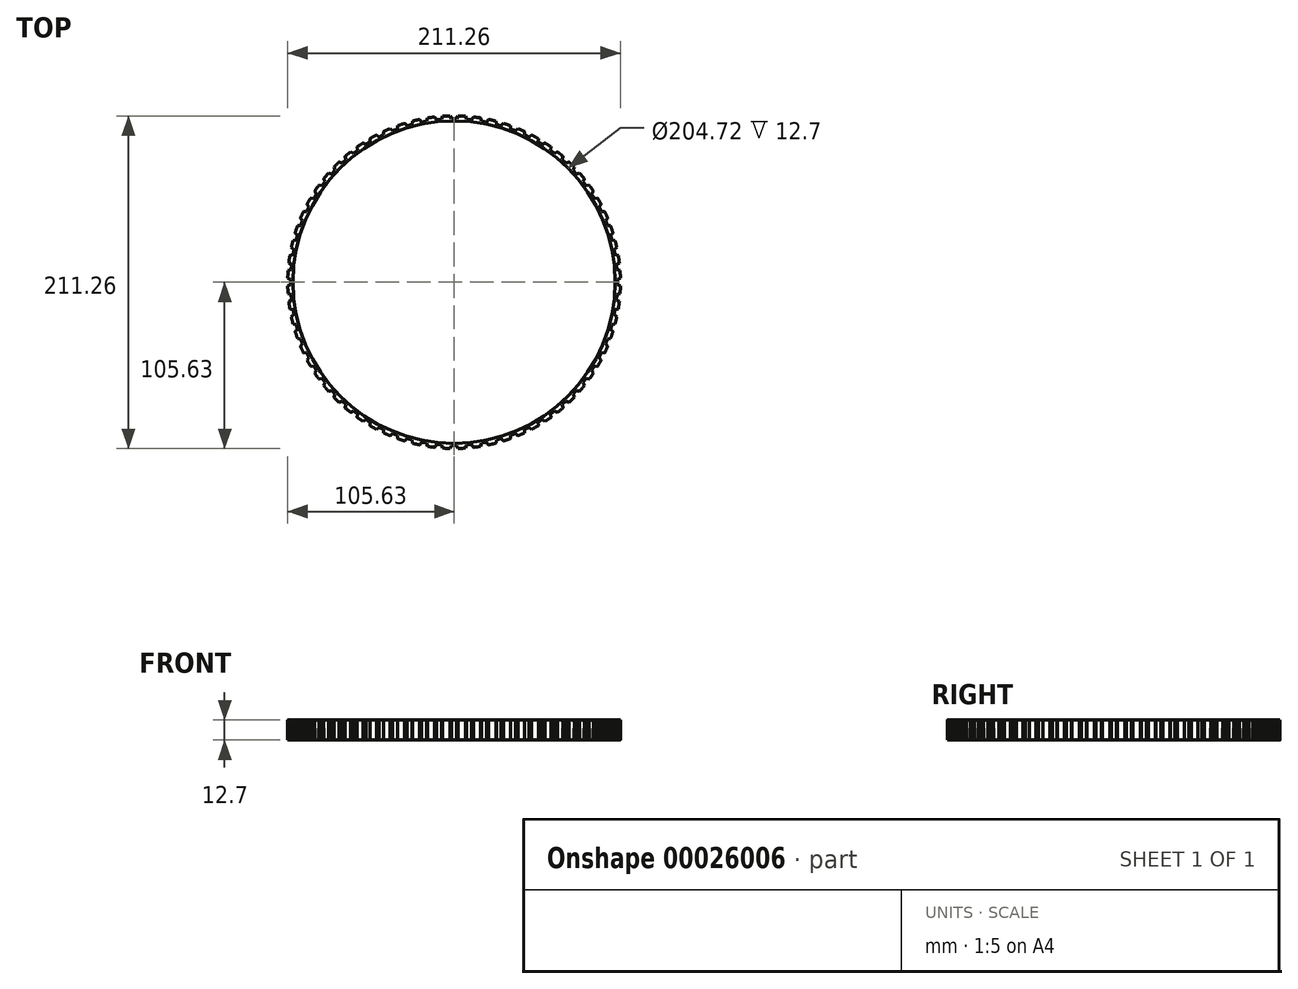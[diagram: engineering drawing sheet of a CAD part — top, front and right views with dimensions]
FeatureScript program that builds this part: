
annotation { "Feature Type Name" : "Feature", "Feature Type Description" : "" }
export const myFeature = defineFeature(function(context is Context, id is Id, definition is map)
    precondition{}
    {
        {
            var Q0;
            Q0=qCreatedBy(makeId("Top.planeOp"),FACE);
            var sketch = newSketch(context, id + "F0", { "sketchPlane" : qUnion([Q0])});
            skCircle(sketch, "E0", {"center": v(0, 0) * mm, "radius": 103.76 * mm, "construction": true});
            skCircle(sketch, "E1", {"center": v(0, 0) * mm, "radius": 102.36 * mm});
            skCircle(sketch, "E2", {"center": v(0, 0) * mm, "radius": 105.66 * mm});
            skSolve(sketch);
        }
        {
            var Q0;
            Q0=qSketchRegion(id+"F0",true);
            extrude(context, id + "F1", {"entities" : qUnion([Q0]), "depth" : 12.7 * mm});
        }
        {
            var Q0;
            Q0=makeQuery(id+"F1.opExtrude","CAP_FACE",FACE,{"disambiguationData":[OSD([sQuery(id+"F0.wireOp",EDGE,"E1"),sQuery(id+"F0.wireOp",EDGE,"E2")])],"isStart":false});
            var sketch = newSketch(context, id + "F2", { "sketchPlane" : qUnion([Q0])});
            skLineSegment(sketch, "E3", {"start": v(0, 0) * mm, "end": v(0, 103.76) * mm, "construction": true});
            skLineSegment(sketch, "E4", {"start": v(-1.63, 103.76) * mm, "end": v(1.63, 103.76) * mm});
            skLineSegment(sketch, "E5", {"start": v(-1.63, 103.76) * mm, "end": v(-3.2, 107.13) * mm});
            skLineSegment(sketch, "E6", {"start": v(1.63, 103.76) * mm, "end": v(3.2, 107.13) * mm});
            skLineSegment(sketch, "E7", {"start": v(3.2, 107.13) * mm, "end": v(-3.2, 107.13) * mm});
            skLineSegment(sketch, "E8", {"start": v(0, 103.76) * mm, "end": v(0, 107.13) * mm, "construction": true});
            skLineSegment(sketch, "E9.1.2", {"start": v(-11.2, 103.17) * mm, "end": v(-13.07, 106.38) * mm});
            skLineSegment(sketch, "E9.1.3", {"start": v(-11.2, 103.17) * mm, "end": v(-7.96, 103.47) * mm});
            skLineSegment(sketch, "E9.1.7", {"start": v(-7.96, 103.47) * mm, "end": v(-6.7, 106.97) * mm});
            skLineSegment(sketch, "E9.1.8", {"start": v(-6.7, 106.97) * mm, "end": v(-13.07, 106.38) * mm});
            skLineSegment(sketch, "E9.2.2", {"start": v(-20.66, 101.7) * mm, "end": v(-22.83, 104.72) * mm});
            skLineSegment(sketch, "E9.2.3", {"start": v(-20.66, 101.7) * mm, "end": v(-17.47, 102.3) * mm});
            skLineSegment(sketch, "E9.2.7", {"start": v(-17.47, 102.3) * mm, "end": v(-16.54, 105.9) * mm});
            skLineSegment(sketch, "E9.2.8", {"start": v(-16.54, 105.9) * mm, "end": v(-22.83, 104.72) * mm});
            skLineSegment(sketch, "E9.3.2", {"start": v(-29.96, 99.35) * mm, "end": v(-32.4, 102.17) * mm});
            skLineSegment(sketch, "E9.3.3", {"start": v(-29.96, 99.35) * mm, "end": v(-26.83, 100.24) * mm});
            skLineSegment(sketch, "E9.3.7", {"start": v(-26.83, 100.24) * mm, "end": v(-26.24, 103.92) * mm});
            skLineSegment(sketch, "E9.3.8", {"start": v(-26.24, 103.92) * mm, "end": v(-32.4, 102.17) * mm});
            skLineSegment(sketch, "E9.4.2", {"start": v(-39, 96.17) * mm, "end": v(-41.68, 98.74) * mm});
            skLineSegment(sketch, "E9.4.3", {"start": v(-39, 96.17) * mm, "end": v(-35.97, 97.34) * mm});
            skLineSegment(sketch, "E9.4.7", {"start": v(-35.97, 97.34) * mm, "end": v(-35.72, 101.05) * mm});
            skLineSegment(sketch, "E9.4.8", {"start": v(-35.72, 101.05) * mm, "end": v(-41.68, 98.74) * mm});
            skLineSegment(sketch, "E9.5.2", {"start": v(-47.7, 92.16) * mm, "end": v(-50.61, 94.47) * mm});
            skLineSegment(sketch, "E9.5.3", {"start": v(-47.7, 92.16) * mm, "end": v(-44.8, 93.6) * mm});
            skLineSegment(sketch, "E9.5.7", {"start": v(-44.8, 93.6) * mm, "end": v(-44.89, 97.32) * mm});
            skLineSegment(sketch, "E9.5.8", {"start": v(-44.89, 97.32) * mm, "end": v(-50.61, 94.47) * mm});
            skLineSegment(sketch, "E9.6.2", {"start": v(-56, 87.36) * mm, "end": v(-59.12, 89.4) * mm});
            skLineSegment(sketch, "E9.6.3", {"start": v(-56, 87.36) * mm, "end": v(-53.24, 89.07) * mm});
            skLineSegment(sketch, "E9.6.7", {"start": v(-53.24, 89.07) * mm, "end": v(-53.68, 92.77) * mm});
            skLineSegment(sketch, "E9.6.8", {"start": v(-53.68, 92.77) * mm, "end": v(-59.12, 89.4) * mm});
            skLineSegment(sketch, "E9.7.2", {"start": v(-63.83, 81.82) * mm, "end": v(-67.11, 83.57) * mm});
            skLineSegment(sketch, "E9.7.3", {"start": v(-63.83, 81.82) * mm, "end": v(-61.23, 83.78) * mm});
            skLineSegment(sketch, "E9.7.7", {"start": v(-61.23, 83.78) * mm, "end": v(-62, 87.42) * mm});
            skLineSegment(sketch, "E9.7.8", {"start": v(-62, 87.42) * mm, "end": v(-67.11, 83.57) * mm});
            skLineSegment(sketch, "E9.8.2", {"start": v(-71.1, 75.58) * mm, "end": v(-74.54, 77.02) * mm});
            skLineSegment(sketch, "E9.8.3", {"start": v(-71.1, 75.58) * mm, "end": v(-68.7, 77.77) * mm});
            skLineSegment(sketch, "E9.8.7", {"start": v(-68.7, 77.77) * mm, "end": v(-69.81, 81.32) * mm});
            skLineSegment(sketch, "E9.8.8", {"start": v(-69.81, 81.32) * mm, "end": v(-74.54, 77.02) * mm});
            skLineSegment(sketch, "E9.9.2", {"start": v(-77.77, 68.7) * mm, "end": v(-81.32, 69.81) * mm});
            skLineSegment(sketch, "E9.9.3", {"start": v(-77.77, 68.7) * mm, "end": v(-75.58, 71.1) * mm});
            skLineSegment(sketch, "E9.9.7", {"start": v(-75.58, 71.1) * mm, "end": v(-77.02, 74.54) * mm});
            skLineSegment(sketch, "E9.9.8", {"start": v(-77.02, 74.54) * mm, "end": v(-81.32, 69.81) * mm});
            skLineSegment(sketch, "E9.10.2", {"start": v(-83.78, 61.23) * mm, "end": v(-87.42, 62) * mm});
            skLineSegment(sketch, "E9.10.3", {"start": v(-83.78, 61.23) * mm, "end": v(-81.82, 63.83) * mm});
            skLineSegment(sketch, "E9.10.7", {"start": v(-81.82, 63.83) * mm, "end": v(-83.57, 67.11) * mm});
            skLineSegment(sketch, "E9.10.8", {"start": v(-83.57, 67.11) * mm, "end": v(-87.42, 62) * mm});
            skLineSegment(sketch, "E9.11.2", {"start": v(-89.07, 53.24) * mm, "end": v(-92.77, 53.68) * mm});
            skLineSegment(sketch, "E9.11.3", {"start": v(-89.07, 53.24) * mm, "end": v(-87.36, 56) * mm});
            skLineSegment(sketch, "E9.11.7", {"start": v(-87.36, 56) * mm, "end": v(-89.4, 59.12) * mm});
            skLineSegment(sketch, "E9.11.8", {"start": v(-89.4, 59.12) * mm, "end": v(-92.77, 53.68) * mm});
            skLineSegment(sketch, "E9.12.2", {"start": v(-93.6, 44.8) * mm, "end": v(-97.32, 44.89) * mm});
            skLineSegment(sketch, "E9.12.3", {"start": v(-93.6, 44.8) * mm, "end": v(-92.16, 47.7) * mm});
            skLineSegment(sketch, "E9.12.7", {"start": v(-92.16, 47.7) * mm, "end": v(-94.47, 50.61) * mm});
            skLineSegment(sketch, "E9.12.8", {"start": v(-94.47, 50.61) * mm, "end": v(-97.32, 44.89) * mm});
            skLineSegment(sketch, "E9.13.2", {"start": v(-97.34, 35.97) * mm, "end": v(-101.05, 35.72) * mm});
            skLineSegment(sketch, "E9.13.3", {"start": v(-97.34, 35.97) * mm, "end": v(-96.17, 39) * mm});
            skLineSegment(sketch, "E9.13.7", {"start": v(-96.17, 39) * mm, "end": v(-98.74, 41.68) * mm});
            skLineSegment(sketch, "E9.13.8", {"start": v(-98.74, 41.68) * mm, "end": v(-101.05, 35.72) * mm});
            skLineSegment(sketch, "E9.14.2", {"start": v(-100.24, 26.83) * mm, "end": v(-103.92, 26.24) * mm});
            skLineSegment(sketch, "E9.14.3", {"start": v(-100.24, 26.83) * mm, "end": v(-99.35, 29.96) * mm});
            skLineSegment(sketch, "E9.14.7", {"start": v(-99.35, 29.96) * mm, "end": v(-102.17, 32.4) * mm});
            skLineSegment(sketch, "E9.14.8", {"start": v(-102.17, 32.4) * mm, "end": v(-103.92, 26.24) * mm});
            skLineSegment(sketch, "E9.15.2", {"start": v(-102.3, 17.47) * mm, "end": v(-105.9, 16.54) * mm});
            skLineSegment(sketch, "E9.15.3", {"start": v(-102.3, 17.47) * mm, "end": v(-101.7, 20.66) * mm});
            skLineSegment(sketch, "E9.15.7", {"start": v(-101.7, 20.66) * mm, "end": v(-104.72, 22.83) * mm});
            skLineSegment(sketch, "E9.15.8", {"start": v(-104.72, 22.83) * mm, "end": v(-105.9, 16.54) * mm});
            skLineSegment(sketch, "E9.16.2", {"start": v(-103.47, 7.96) * mm, "end": v(-106.97, 6.7) * mm});
            skLineSegment(sketch, "E9.16.3", {"start": v(-103.47, 7.96) * mm, "end": v(-103.17, 11.2) * mm});
            skLineSegment(sketch, "E9.16.7", {"start": v(-103.17, 11.2) * mm, "end": v(-106.38, 13.07) * mm});
            skLineSegment(sketch, "E9.16.8", {"start": v(-106.38, 13.07) * mm, "end": v(-106.97, 6.7) * mm});
            skLineSegment(sketch, "E9.17.2", {"start": v(-103.76, -1.63) * mm, "end": v(-107.13, -3.2) * mm});
            skLineSegment(sketch, "E9.17.3", {"start": v(-103.76, -1.63) * mm, "end": v(-103.76, 1.63) * mm});
            skLineSegment(sketch, "E9.17.7", {"start": v(-103.76, 1.63) * mm, "end": v(-107.13, 3.2) * mm});
            skLineSegment(sketch, "E9.17.8", {"start": v(-107.13, 3.2) * mm, "end": v(-107.13, -3.2) * mm});
            skLineSegment(sketch, "E9.18.2", {"start": v(-103.17, -11.2) * mm, "end": v(-106.38, -13.07) * mm});
            skLineSegment(sketch, "E9.18.3", {"start": v(-103.17, -11.2) * mm, "end": v(-103.47, -7.96) * mm});
            skLineSegment(sketch, "E9.18.7", {"start": v(-103.47, -7.96) * mm, "end": v(-106.97, -6.7) * mm});
            skLineSegment(sketch, "E9.18.8", {"start": v(-106.97, -6.7) * mm, "end": v(-106.38, -13.07) * mm});
            skLineSegment(sketch, "E9.19.2", {"start": v(-101.7, -20.66) * mm, "end": v(-104.72, -22.83) * mm});
            skLineSegment(sketch, "E9.19.3", {"start": v(-101.7, -20.66) * mm, "end": v(-102.3, -17.47) * mm});
            skLineSegment(sketch, "E9.19.7", {"start": v(-102.3, -17.47) * mm, "end": v(-105.9, -16.54) * mm});
            skLineSegment(sketch, "E9.19.8", {"start": v(-105.9, -16.54) * mm, "end": v(-104.72, -22.83) * mm});
            skLineSegment(sketch, "E9.20.2", {"start": v(-99.35, -29.96) * mm, "end": v(-102.17, -32.4) * mm});
            skLineSegment(sketch, "E9.20.3", {"start": v(-99.35, -29.96) * mm, "end": v(-100.24, -26.83) * mm});
            skLineSegment(sketch, "E9.20.7", {"start": v(-100.24, -26.83) * mm, "end": v(-103.92, -26.24) * mm});
            skLineSegment(sketch, "E9.20.8", {"start": v(-103.92, -26.24) * mm, "end": v(-102.17, -32.4) * mm});
            skLineSegment(sketch, "E9.21.2", {"start": v(-96.17, -39) * mm, "end": v(-98.74, -41.68) * mm});
            skLineSegment(sketch, "E9.21.3", {"start": v(-96.17, -39) * mm, "end": v(-97.34, -35.97) * mm});
            skLineSegment(sketch, "E9.21.7", {"start": v(-97.34, -35.97) * mm, "end": v(-101.05, -35.72) * mm});
            skLineSegment(sketch, "E9.21.8", {"start": v(-101.05, -35.72) * mm, "end": v(-98.74, -41.68) * mm});
            skLineSegment(sketch, "E9.22.2", {"start": v(-92.16, -47.7) * mm, "end": v(-94.47, -50.61) * mm});
            skLineSegment(sketch, "E9.22.3", {"start": v(-92.16, -47.7) * mm, "end": v(-93.6, -44.8) * mm});
            skLineSegment(sketch, "E9.22.7", {"start": v(-93.6, -44.8) * mm, "end": v(-97.32, -44.89) * mm});
            skLineSegment(sketch, "E9.22.8", {"start": v(-97.32, -44.89) * mm, "end": v(-94.47, -50.61) * mm});
            skLineSegment(sketch, "E9.23.2", {"start": v(-87.36, -56) * mm, "end": v(-89.4, -59.12) * mm});
            skLineSegment(sketch, "E9.23.3", {"start": v(-87.36, -56) * mm, "end": v(-89.07, -53.24) * mm});
            skLineSegment(sketch, "E9.23.7", {"start": v(-89.07, -53.24) * mm, "end": v(-92.77, -53.68) * mm});
            skLineSegment(sketch, "E9.23.8", {"start": v(-92.77, -53.68) * mm, "end": v(-89.4, -59.12) * mm});
            skLineSegment(sketch, "E9.24.2", {"start": v(-81.82, -63.83) * mm, "end": v(-83.57, -67.11) * mm});
            skLineSegment(sketch, "E9.24.3", {"start": v(-81.82, -63.83) * mm, "end": v(-83.78, -61.23) * mm});
            skLineSegment(sketch, "E9.24.7", {"start": v(-83.78, -61.23) * mm, "end": v(-87.42, -62) * mm});
            skLineSegment(sketch, "E9.24.8", {"start": v(-87.42, -62) * mm, "end": v(-83.57, -67.11) * mm});
            skLineSegment(sketch, "E9.25.2", {"start": v(-75.58, -71.1) * mm, "end": v(-77.02, -74.54) * mm});
            skLineSegment(sketch, "E9.25.3", {"start": v(-75.58, -71.1) * mm, "end": v(-77.77, -68.7) * mm});
            skLineSegment(sketch, "E9.25.7", {"start": v(-77.77, -68.7) * mm, "end": v(-81.32, -69.81) * mm});
            skLineSegment(sketch, "E9.25.8", {"start": v(-81.32, -69.81) * mm, "end": v(-77.02, -74.54) * mm});
            skLineSegment(sketch, "E9.26.2", {"start": v(-68.7, -77.77) * mm, "end": v(-69.81, -81.32) * mm});
            skLineSegment(sketch, "E9.26.3", {"start": v(-68.7, -77.77) * mm, "end": v(-71.1, -75.58) * mm});
            skLineSegment(sketch, "E9.26.7", {"start": v(-71.1, -75.58) * mm, "end": v(-74.54, -77.02) * mm});
            skLineSegment(sketch, "E9.26.8", {"start": v(-74.54, -77.02) * mm, "end": v(-69.81, -81.32) * mm});
            skLineSegment(sketch, "E9.27.2", {"start": v(-61.23, -83.78) * mm, "end": v(-62, -87.42) * mm});
            skLineSegment(sketch, "E9.27.3", {"start": v(-61.23, -83.78) * mm, "end": v(-63.83, -81.82) * mm});
            skLineSegment(sketch, "E9.27.7", {"start": v(-63.83, -81.82) * mm, "end": v(-67.11, -83.57) * mm});
            skLineSegment(sketch, "E9.27.8", {"start": v(-67.11, -83.57) * mm, "end": v(-62, -87.42) * mm});
            skLineSegment(sketch, "E9.28.2", {"start": v(-53.24, -89.07) * mm, "end": v(-53.68, -92.77) * mm});
            skLineSegment(sketch, "E9.28.3", {"start": v(-53.24, -89.07) * mm, "end": v(-56, -87.36) * mm});
            skLineSegment(sketch, "E9.28.7", {"start": v(-56, -87.36) * mm, "end": v(-59.12, -89.4) * mm});
            skLineSegment(sketch, "E9.28.8", {"start": v(-59.12, -89.4) * mm, "end": v(-53.68, -92.77) * mm});
            skLineSegment(sketch, "E9.29.2", {"start": v(-44.8, -93.6) * mm, "end": v(-44.89, -97.32) * mm});
            skLineSegment(sketch, "E9.29.3", {"start": v(-44.8, -93.6) * mm, "end": v(-47.7, -92.16) * mm});
            skLineSegment(sketch, "E9.29.7", {"start": v(-47.7, -92.16) * mm, "end": v(-50.61, -94.47) * mm});
            skLineSegment(sketch, "E9.29.8", {"start": v(-50.61, -94.47) * mm, "end": v(-44.89, -97.32) * mm});
            skLineSegment(sketch, "E9.30.2", {"start": v(-35.97, -97.34) * mm, "end": v(-35.72, -101.05) * mm});
            skLineSegment(sketch, "E9.30.3", {"start": v(-35.97, -97.34) * mm, "end": v(-39, -96.17) * mm});
            skLineSegment(sketch, "E9.30.7", {"start": v(-39, -96.17) * mm, "end": v(-41.68, -98.74) * mm});
            skLineSegment(sketch, "E9.30.8", {"start": v(-41.68, -98.74) * mm, "end": v(-35.72, -101.05) * mm});
            skLineSegment(sketch, "E9.31.2", {"start": v(-26.83, -100.24) * mm, "end": v(-26.24, -103.92) * mm});
            skLineSegment(sketch, "E9.31.3", {"start": v(-26.83, -100.24) * mm, "end": v(-29.96, -99.35) * mm});
            skLineSegment(sketch, "E9.31.7", {"start": v(-29.96, -99.35) * mm, "end": v(-32.4, -102.17) * mm});
            skLineSegment(sketch, "E9.31.8", {"start": v(-32.4, -102.17) * mm, "end": v(-26.24, -103.92) * mm});
            skLineSegment(sketch, "E9.32.2", {"start": v(-17.47, -102.3) * mm, "end": v(-16.54, -105.9) * mm});
            skLineSegment(sketch, "E9.32.3", {"start": v(-17.47, -102.3) * mm, "end": v(-20.66, -101.7) * mm});
            skLineSegment(sketch, "E9.32.7", {"start": v(-20.66, -101.7) * mm, "end": v(-22.83, -104.72) * mm});
            skLineSegment(sketch, "E9.32.8", {"start": v(-22.83, -104.72) * mm, "end": v(-16.54, -105.9) * mm});
            skLineSegment(sketch, "E9.33.2", {"start": v(-7.96, -103.47) * mm, "end": v(-6.7, -106.97) * mm});
            skLineSegment(sketch, "E9.33.3", {"start": v(-7.96, -103.47) * mm, "end": v(-11.2, -103.17) * mm});
            skLineSegment(sketch, "E9.33.7", {"start": v(-11.2, -103.17) * mm, "end": v(-13.07, -106.38) * mm});
            skLineSegment(sketch, "E9.33.8", {"start": v(-13.07, -106.38) * mm, "end": v(-6.7, -106.97) * mm});
            skLineSegment(sketch, "E9.34.2", {"start": v(1.63, -103.76) * mm, "end": v(3.2, -107.13) * mm});
            skLineSegment(sketch, "E9.34.3", {"start": v(1.63, -103.76) * mm, "end": v(-1.63, -103.76) * mm});
            skLineSegment(sketch, "E9.34.7", {"start": v(-1.63, -103.76) * mm, "end": v(-3.2, -107.13) * mm});
            skLineSegment(sketch, "E9.34.8", {"start": v(-3.2, -107.13) * mm, "end": v(3.2, -107.13) * mm});
            skLineSegment(sketch, "E9.35.2", {"start": v(11.2, -103.17) * mm, "end": v(13.07, -106.38) * mm});
            skLineSegment(sketch, "E9.35.3", {"start": v(11.2, -103.17) * mm, "end": v(7.96, -103.47) * mm});
            skLineSegment(sketch, "E9.35.7", {"start": v(7.96, -103.47) * mm, "end": v(6.7, -106.97) * mm});
            skLineSegment(sketch, "E9.35.8", {"start": v(6.7, -106.97) * mm, "end": v(13.07, -106.38) * mm});
            skLineSegment(sketch, "E9.36.2", {"start": v(20.66, -101.7) * mm, "end": v(22.83, -104.72) * mm});
            skLineSegment(sketch, "E9.36.3", {"start": v(20.66, -101.7) * mm, "end": v(17.47, -102.3) * mm});
            skLineSegment(sketch, "E9.36.7", {"start": v(17.47, -102.3) * mm, "end": v(16.54, -105.9) * mm});
            skLineSegment(sketch, "E9.36.8", {"start": v(16.54, -105.9) * mm, "end": v(22.83, -104.72) * mm});
            skLineSegment(sketch, "E9.37.2", {"start": v(29.96, -99.35) * mm, "end": v(32.4, -102.17) * mm});
            skLineSegment(sketch, "E9.37.3", {"start": v(29.96, -99.35) * mm, "end": v(26.83, -100.24) * mm});
            skLineSegment(sketch, "E9.37.7", {"start": v(26.83, -100.24) * mm, "end": v(26.24, -103.92) * mm});
            skLineSegment(sketch, "E9.37.8", {"start": v(26.24, -103.92) * mm, "end": v(32.4, -102.17) * mm});
            skLineSegment(sketch, "E9.38.2", {"start": v(39, -96.17) * mm, "end": v(41.68, -98.74) * mm});
            skLineSegment(sketch, "E9.38.3", {"start": v(39, -96.17) * mm, "end": v(35.97, -97.34) * mm});
            skLineSegment(sketch, "E9.38.7", {"start": v(35.97, -97.34) * mm, "end": v(35.72, -101.05) * mm});
            skLineSegment(sketch, "E9.38.8", {"start": v(35.72, -101.05) * mm, "end": v(41.68, -98.74) * mm});
            skLineSegment(sketch, "E9.39.2", {"start": v(47.7, -92.16) * mm, "end": v(50.61, -94.47) * mm});
            skLineSegment(sketch, "E9.39.3", {"start": v(47.7, -92.16) * mm, "end": v(44.8, -93.6) * mm});
            skLineSegment(sketch, "E9.39.7", {"start": v(44.8, -93.6) * mm, "end": v(44.89, -97.32) * mm});
            skLineSegment(sketch, "E9.39.8", {"start": v(44.89, -97.32) * mm, "end": v(50.61, -94.47) * mm});
            skLineSegment(sketch, "E9.40.2", {"start": v(56, -87.36) * mm, "end": v(59.12, -89.4) * mm});
            skLineSegment(sketch, "E9.40.3", {"start": v(56, -87.36) * mm, "end": v(53.24, -89.07) * mm});
            skLineSegment(sketch, "E9.40.7", {"start": v(53.24, -89.07) * mm, "end": v(53.68, -92.77) * mm});
            skLineSegment(sketch, "E9.40.8", {"start": v(53.68, -92.77) * mm, "end": v(59.12, -89.4) * mm});
            skLineSegment(sketch, "E9.41.2", {"start": v(63.83, -81.82) * mm, "end": v(67.11, -83.57) * mm});
            skLineSegment(sketch, "E9.41.3", {"start": v(63.83, -81.82) * mm, "end": v(61.23, -83.78) * mm});
            skLineSegment(sketch, "E9.41.7", {"start": v(61.23, -83.78) * mm, "end": v(62, -87.42) * mm});
            skLineSegment(sketch, "E9.41.8", {"start": v(62, -87.42) * mm, "end": v(67.11, -83.57) * mm});
            skLineSegment(sketch, "E9.42.2", {"start": v(71.1, -75.58) * mm, "end": v(74.54, -77.02) * mm});
            skLineSegment(sketch, "E9.42.3", {"start": v(71.1, -75.58) * mm, "end": v(68.7, -77.77) * mm});
            skLineSegment(sketch, "E9.42.7", {"start": v(68.7, -77.77) * mm, "end": v(69.81, -81.32) * mm});
            skLineSegment(sketch, "E9.42.8", {"start": v(69.81, -81.32) * mm, "end": v(74.54, -77.02) * mm});
            skLineSegment(sketch, "E9.43.2", {"start": v(77.77, -68.7) * mm, "end": v(81.32, -69.81) * mm});
            skLineSegment(sketch, "E9.43.3", {"start": v(77.77, -68.7) * mm, "end": v(75.58, -71.1) * mm});
            skLineSegment(sketch, "E9.43.7", {"start": v(75.58, -71.1) * mm, "end": v(77.02, -74.54) * mm});
            skLineSegment(sketch, "E9.43.8", {"start": v(77.02, -74.54) * mm, "end": v(81.32, -69.81) * mm});
            skLineSegment(sketch, "E9.44.2", {"start": v(83.78, -61.23) * mm, "end": v(87.42, -62) * mm});
            skLineSegment(sketch, "E9.44.3", {"start": v(83.78, -61.23) * mm, "end": v(81.82, -63.83) * mm});
            skLineSegment(sketch, "E9.44.7", {"start": v(81.82, -63.83) * mm, "end": v(83.57, -67.11) * mm});
            skLineSegment(sketch, "E9.44.8", {"start": v(83.57, -67.11) * mm, "end": v(87.42, -62) * mm});
            skLineSegment(sketch, "E9.45.2", {"start": v(89.07, -53.24) * mm, "end": v(92.77, -53.68) * mm});
            skLineSegment(sketch, "E9.45.3", {"start": v(89.07, -53.24) * mm, "end": v(87.36, -56) * mm});
            skLineSegment(sketch, "E9.45.7", {"start": v(87.36, -56) * mm, "end": v(89.4, -59.12) * mm});
            skLineSegment(sketch, "E9.45.8", {"start": v(89.4, -59.12) * mm, "end": v(92.77, -53.68) * mm});
            skLineSegment(sketch, "E9.46.2", {"start": v(93.6, -44.8) * mm, "end": v(97.32, -44.89) * mm});
            skLineSegment(sketch, "E9.46.3", {"start": v(93.6, -44.8) * mm, "end": v(92.16, -47.7) * mm});
            skLineSegment(sketch, "E9.46.7", {"start": v(92.16, -47.7) * mm, "end": v(94.47, -50.61) * mm});
            skLineSegment(sketch, "E9.46.8", {"start": v(94.47, -50.61) * mm, "end": v(97.32, -44.89) * mm});
            skLineSegment(sketch, "E9.47.2", {"start": v(97.34, -35.97) * mm, "end": v(101.05, -35.72) * mm});
            skLineSegment(sketch, "E9.47.3", {"start": v(97.34, -35.97) * mm, "end": v(96.17, -39) * mm});
            skLineSegment(sketch, "E9.47.7", {"start": v(96.17, -39) * mm, "end": v(98.74, -41.68) * mm});
            skLineSegment(sketch, "E9.47.8", {"start": v(98.74, -41.68) * mm, "end": v(101.05, -35.72) * mm});
            skLineSegment(sketch, "E9.48.2", {"start": v(100.24, -26.83) * mm, "end": v(103.92, -26.24) * mm});
            skLineSegment(sketch, "E9.48.3", {"start": v(100.24, -26.83) * mm, "end": v(99.35, -29.96) * mm});
            skLineSegment(sketch, "E9.48.7", {"start": v(99.35, -29.96) * mm, "end": v(102.17, -32.4) * mm});
            skLineSegment(sketch, "E9.48.8", {"start": v(102.17, -32.4) * mm, "end": v(103.92, -26.24) * mm});
            skLineSegment(sketch, "E9.49.2", {"start": v(102.3, -17.47) * mm, "end": v(105.9, -16.54) * mm});
            skLineSegment(sketch, "E9.49.3", {"start": v(102.3, -17.47) * mm, "end": v(101.7, -20.66) * mm});
            skLineSegment(sketch, "E9.49.7", {"start": v(101.7, -20.66) * mm, "end": v(104.72, -22.83) * mm});
            skLineSegment(sketch, "E9.49.8", {"start": v(104.72, -22.83) * mm, "end": v(105.9, -16.54) * mm});
            skLineSegment(sketch, "E9.50.2", {"start": v(103.47, -7.96) * mm, "end": v(106.97, -6.7) * mm});
            skLineSegment(sketch, "E9.50.3", {"start": v(103.47, -7.96) * mm, "end": v(103.17, -11.2) * mm});
            skLineSegment(sketch, "E9.50.7", {"start": v(103.17, -11.2) * mm, "end": v(106.38, -13.07) * mm});
            skLineSegment(sketch, "E9.50.8", {"start": v(106.38, -13.07) * mm, "end": v(106.97, -6.7) * mm});
            skLineSegment(sketch, "E9.51.2", {"start": v(103.76, 1.63) * mm, "end": v(107.13, 3.2) * mm});
            skLineSegment(sketch, "E9.51.3", {"start": v(103.76, 1.63) * mm, "end": v(103.76, -1.63) * mm});
            skLineSegment(sketch, "E9.51.7", {"start": v(103.76, -1.63) * mm, "end": v(107.13, -3.2) * mm});
            skLineSegment(sketch, "E9.51.8", {"start": v(107.13, -3.2) * mm, "end": v(107.13, 3.2) * mm});
            skLineSegment(sketch, "E9.52.2", {"start": v(103.17, 11.2) * mm, "end": v(106.38, 13.07) * mm});
            skLineSegment(sketch, "E9.52.3", {"start": v(103.17, 11.2) * mm, "end": v(103.47, 7.96) * mm});
            skLineSegment(sketch, "E9.52.7", {"start": v(103.47, 7.96) * mm, "end": v(106.97, 6.7) * mm});
            skLineSegment(sketch, "E9.52.8", {"start": v(106.97, 6.7) * mm, "end": v(106.38, 13.07) * mm});
            skLineSegment(sketch, "E9.53.2", {"start": v(101.7, 20.66) * mm, "end": v(104.72, 22.83) * mm});
            skLineSegment(sketch, "E9.53.3", {"start": v(101.7, 20.66) * mm, "end": v(102.3, 17.47) * mm});
            skLineSegment(sketch, "E9.53.7", {"start": v(102.3, 17.47) * mm, "end": v(105.9, 16.54) * mm});
            skLineSegment(sketch, "E9.53.8", {"start": v(105.9, 16.54) * mm, "end": v(104.72, 22.83) * mm});
            skLineSegment(sketch, "E9.54.2", {"start": v(99.35, 29.96) * mm, "end": v(102.17, 32.4) * mm});
            skLineSegment(sketch, "E9.54.3", {"start": v(99.35, 29.96) * mm, "end": v(100.24, 26.83) * mm});
            skLineSegment(sketch, "E9.54.7", {"start": v(100.24, 26.83) * mm, "end": v(103.92, 26.24) * mm});
            skLineSegment(sketch, "E9.54.8", {"start": v(103.92, 26.24) * mm, "end": v(102.17, 32.4) * mm});
            skLineSegment(sketch, "E9.55.2", {"start": v(96.17, 39) * mm, "end": v(98.74, 41.68) * mm});
            skLineSegment(sketch, "E9.55.3", {"start": v(96.17, 39) * mm, "end": v(97.34, 35.97) * mm});
            skLineSegment(sketch, "E9.55.7", {"start": v(97.34, 35.97) * mm, "end": v(101.05, 35.72) * mm});
            skLineSegment(sketch, "E9.55.8", {"start": v(101.05, 35.72) * mm, "end": v(98.74, 41.68) * mm});
            skLineSegment(sketch, "E9.56.2", {"start": v(92.16, 47.7) * mm, "end": v(94.47, 50.61) * mm});
            skLineSegment(sketch, "E9.56.3", {"start": v(92.16, 47.7) * mm, "end": v(93.6, 44.8) * mm});
            skLineSegment(sketch, "E9.56.7", {"start": v(93.6, 44.8) * mm, "end": v(97.32, 44.89) * mm});
            skLineSegment(sketch, "E9.56.8", {"start": v(97.32, 44.89) * mm, "end": v(94.47, 50.61) * mm});
            skLineSegment(sketch, "E9.57.2", {"start": v(87.36, 56) * mm, "end": v(89.4, 59.12) * mm});
            skLineSegment(sketch, "E9.57.3", {"start": v(87.36, 56) * mm, "end": v(89.07, 53.24) * mm});
            skLineSegment(sketch, "E9.57.7", {"start": v(89.07, 53.24) * mm, "end": v(92.77, 53.68) * mm});
            skLineSegment(sketch, "E9.57.8", {"start": v(92.77, 53.68) * mm, "end": v(89.4, 59.12) * mm});
            skLineSegment(sketch, "E9.58.2", {"start": v(81.82, 63.83) * mm, "end": v(83.57, 67.11) * mm});
            skLineSegment(sketch, "E9.58.3", {"start": v(81.82, 63.83) * mm, "end": v(83.78, 61.23) * mm});
            skLineSegment(sketch, "E9.58.7", {"start": v(83.78, 61.23) * mm, "end": v(87.42, 62) * mm});
            skLineSegment(sketch, "E9.58.8", {"start": v(87.42, 62) * mm, "end": v(83.57, 67.11) * mm});
            skLineSegment(sketch, "E9.59.2", {"start": v(75.58, 71.1) * mm, "end": v(77.02, 74.54) * mm});
            skLineSegment(sketch, "E9.59.3", {"start": v(75.58, 71.1) * mm, "end": v(77.77, 68.7) * mm});
            skLineSegment(sketch, "E9.59.7", {"start": v(77.77, 68.7) * mm, "end": v(81.32, 69.81) * mm});
            skLineSegment(sketch, "E9.59.8", {"start": v(81.32, 69.81) * mm, "end": v(77.02, 74.54) * mm});
            skLineSegment(sketch, "E9.60.2", {"start": v(68.7, 77.77) * mm, "end": v(69.81, 81.32) * mm});
            skLineSegment(sketch, "E9.60.3", {"start": v(68.7, 77.77) * mm, "end": v(71.1, 75.58) * mm});
            skLineSegment(sketch, "E9.60.7", {"start": v(71.1, 75.58) * mm, "end": v(74.54, 77.02) * mm});
            skLineSegment(sketch, "E9.60.8", {"start": v(74.54, 77.02) * mm, "end": v(69.81, 81.32) * mm});
            skLineSegment(sketch, "E9.61.2", {"start": v(61.23, 83.78) * mm, "end": v(62, 87.42) * mm});
            skLineSegment(sketch, "E9.61.3", {"start": v(61.23, 83.78) * mm, "end": v(63.83, 81.82) * mm});
            skLineSegment(sketch, "E9.61.7", {"start": v(63.83, 81.82) * mm, "end": v(67.11, 83.57) * mm});
            skLineSegment(sketch, "E9.61.8", {"start": v(67.11, 83.57) * mm, "end": v(62, 87.42) * mm});
            skLineSegment(sketch, "E9.62.2", {"start": v(53.24, 89.07) * mm, "end": v(53.68, 92.77) * mm});
            skLineSegment(sketch, "E9.62.3", {"start": v(53.24, 89.07) * mm, "end": v(56, 87.36) * mm});
            skLineSegment(sketch, "E9.62.7", {"start": v(56, 87.36) * mm, "end": v(59.12, 89.4) * mm});
            skLineSegment(sketch, "E9.62.8", {"start": v(59.12, 89.4) * mm, "end": v(53.68, 92.77) * mm});
            skLineSegment(sketch, "E9.63.2", {"start": v(44.8, 93.6) * mm, "end": v(44.89, 97.32) * mm});
            skLineSegment(sketch, "E9.63.3", {"start": v(44.8, 93.6) * mm, "end": v(47.7, 92.16) * mm});
            skLineSegment(sketch, "E9.63.7", {"start": v(47.7, 92.16) * mm, "end": v(50.61, 94.47) * mm});
            skLineSegment(sketch, "E9.63.8", {"start": v(50.61, 94.47) * mm, "end": v(44.89, 97.32) * mm});
            skLineSegment(sketch, "E9.64.2", {"start": v(35.97, 97.34) * mm, "end": v(35.72, 101.05) * mm});
            skLineSegment(sketch, "E9.64.3", {"start": v(35.97, 97.34) * mm, "end": v(39, 96.17) * mm});
            skLineSegment(sketch, "E9.64.7", {"start": v(39, 96.17) * mm, "end": v(41.68, 98.74) * mm});
            skLineSegment(sketch, "E9.64.8", {"start": v(41.68, 98.74) * mm, "end": v(35.72, 101.05) * mm});
            skLineSegment(sketch, "E9.65.2", {"start": v(26.83, 100.24) * mm, "end": v(26.24, 103.92) * mm});
            skLineSegment(sketch, "E9.65.3", {"start": v(26.83, 100.24) * mm, "end": v(29.96, 99.35) * mm});
            skLineSegment(sketch, "E9.65.7", {"start": v(29.96, 99.35) * mm, "end": v(32.4, 102.17) * mm});
            skLineSegment(sketch, "E9.65.8", {"start": v(32.4, 102.17) * mm, "end": v(26.24, 103.92) * mm});
            skLineSegment(sketch, "E9.66.2", {"start": v(17.47, 102.3) * mm, "end": v(16.54, 105.9) * mm});
            skLineSegment(sketch, "E9.66.3", {"start": v(17.47, 102.3) * mm, "end": v(20.66, 101.7) * mm});
            skLineSegment(sketch, "E9.66.7", {"start": v(20.66, 101.7) * mm, "end": v(22.83, 104.72) * mm});
            skLineSegment(sketch, "E9.66.8", {"start": v(22.83, 104.72) * mm, "end": v(16.54, 105.9) * mm});
            skLineSegment(sketch, "E9.67.2", {"start": v(7.96, 103.47) * mm, "end": v(6.7, 106.97) * mm});
            skLineSegment(sketch, "E9.67.3", {"start": v(7.96, 103.47) * mm, "end": v(11.2, 103.17) * mm});
            skLineSegment(sketch, "E9.67.7", {"start": v(11.2, 103.17) * mm, "end": v(13.07, 106.38) * mm});
            skLineSegment(sketch, "E9.67.8", {"start": v(13.07, 106.38) * mm, "end": v(6.7, 106.97) * mm});
            skPoint(sketch, "E9.center", {"position": v(0, 0) * mm});
            skSolve(sketch);
        }
        {
            var Q0;
            Q0=qSketchRegion(id+"F2",true);
            extrude(context, id + "F3", {"entities" : qUnion([Q0]), "operationType" : NewBodyOperationType.REMOVE, "endBound" : BoundingType.THROUGH_ALL, "oppositeDirection" : true, "depth" : 25.4 * mm});
        }
    });
